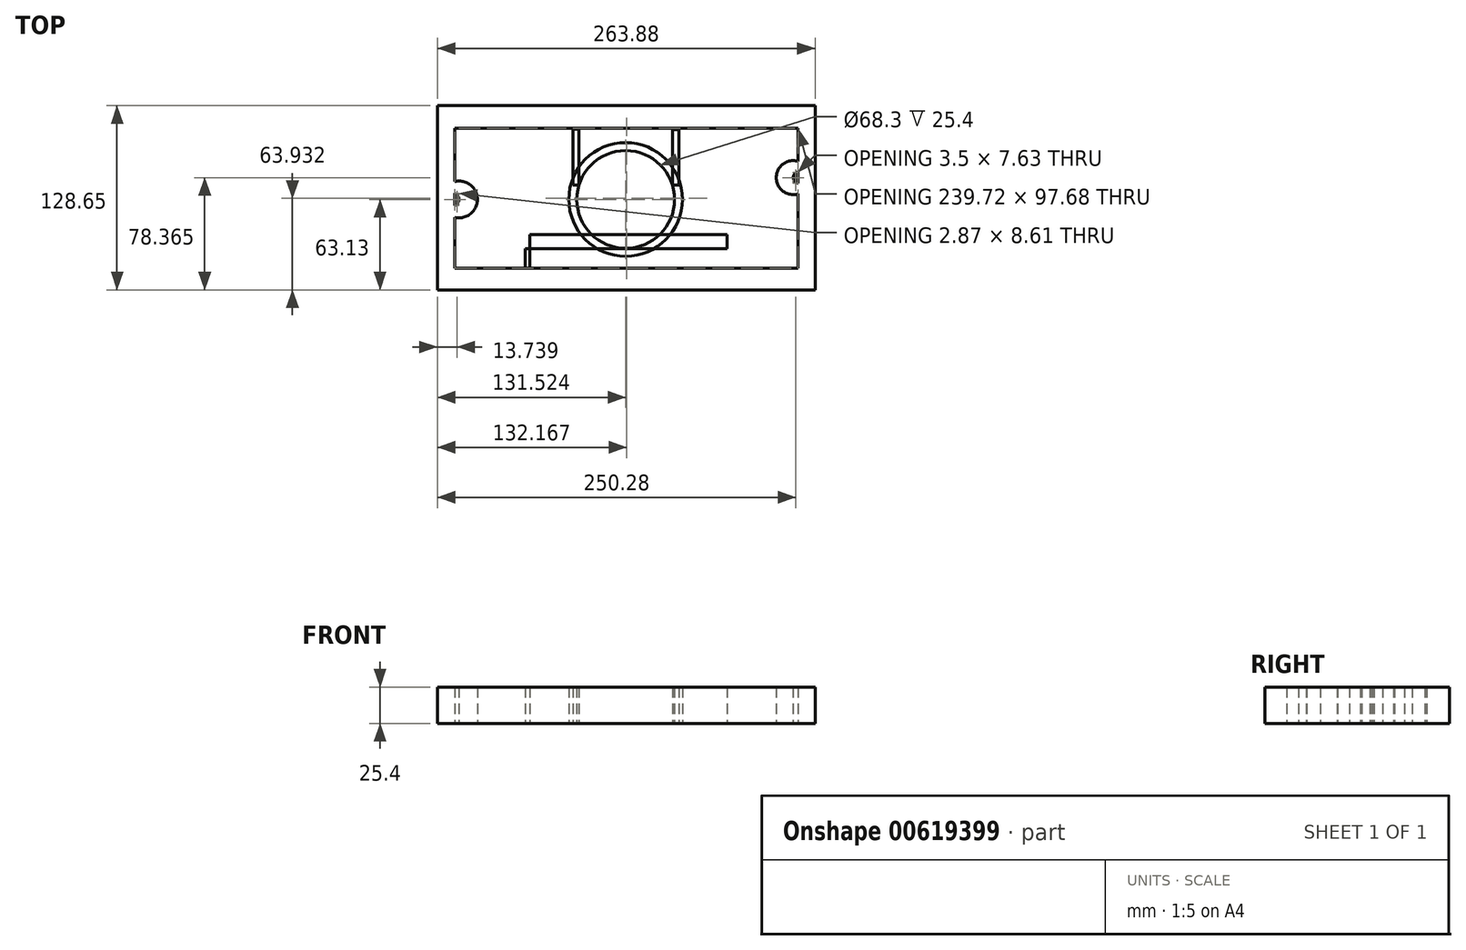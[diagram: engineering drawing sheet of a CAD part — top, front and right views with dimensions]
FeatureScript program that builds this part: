
annotation { "Feature Type Name" : "Feature", "Feature Type Description" : "" }
export const myFeature = defineFeature(function(context is Context, id is Id, definition is map)
    precondition{}
    {
        {
            var Q0;
            Q0=qCreatedBy(makeId("Top.planeOp"),FACE);
            var sketch = newSketch(context, id + "F0", { "sketchPlane" : qUnion([Q0])});
            skLineSegment(sketch, "E0.bottom", {"start": v(-134.85, 65.52) * mm, "end": v(129.03, 65.52) * mm});
            skLineSegment(sketch, "E0.top", {"start": v(-134.85, -63.13) * mm, "end": v(129.03, -63.13) * mm});
            skLineSegment(sketch, "E0.left", {"start": v(-134.85, 65.52) * mm, "end": v(-134.85, -63.13) * mm});
            skLineSegment(sketch, "E0.right", {"start": v(129.03, 65.52) * mm, "end": v(129.03, -63.13) * mm});
            skLineSegment(sketch, "E1.bottom", {"start": v(-122.54, 49.64) * mm, "end": v(117.18, 49.64) * mm});
            skLineSegment(sketch, "E1.top", {"start": v(-122.54, -48.04) * mm, "end": v(117.18, -48.04) * mm});
            skLineSegment(sketch, "E1.left", {"start": v(-122.54, 49.64) * mm, "end": v(-122.54, -48.04) * mm});
            skLineSegment(sketch, "E1.right", {"start": v(117.18, 49.64) * mm, "end": v(117.18, -48.04) * mm});
            skCircle(sketch, "E2", {"center": v(-115.43, 39.12) * mm, "radius": 5.88 * mm});
            skCircle(sketch, "E3", {"center": v(-115.43, -35.95) * mm, "radius": 4.5 * mm});
            skCircle(sketch, "E4", {"center": v(96.35, -31.86) * mm, "radius": 8.34 * mm});
            skCircle(sketch, "E5", {"center": v(97.11, 39.12) * mm, "radius": 6.34 * mm});
            skSolve(sketch);
        }
        {
            var Q0;
            Q0 = qSketchRegion(id + "F0", true);
            extrude(context, id + "F1", {"entities" : qUnion([Q0]), "depth" : 25.4 * mm, "offsetDistance" : 25.4 * mm});
        }
        {
            var Q0;
            Q0=qCreatedBy(makeId("Top.planeOp"),FACE);
            var sketch = newSketch(context, id + "F2", { "sketchPlane" : qUnion([Q0])});
            skCircle(sketch, "E6", {"center": v(-119.68, 43.9) * mm, "radius": 8.1 * mm});
            skCircle(sketch, "E7", {"center": v(-119.68, 43.9) * mm, "radius": 1.6 * mm});
            skCircle(sketch, "E8", {"center": v(82.83, 43.9) * mm, "radius": 9.97 * mm});
            skCircle(sketch, "E9", {"center": v(78.44, 43.9) * mm, "radius": 4.39 * mm});
            skCircle(sketch, "E10", {"center": v(-119.68, 0) * mm, "radius": 12.85 * mm});
            skCircle(sketch, "E11", {"center": v(-124.34, 0) * mm, "radius": 4.66 * mm});
            skCircle(sketch, "E12", {"center": v(77.24, 0) * mm, "radius": 6.36 * mm});
            skCircle(sketch, "E13", {"center": v(77.24, 0) * mm, "radius": 1.01 * mm});
            skSolve(sketch);
        }
        {
            var Q0;
            Q0=makeQuery(id+"F2.imprint","IMPRINT",FACE,{"disambiguationData":[TD([[makeQuery(id+"F2.imprint","IMPRINT",EDGE,{"derivedFrom":sQuery(id+"F2.wireOp",EDGE,"E10")}),1.0]])]});
            extrude(context, id + "F3", {"entities" : qUnion([Q0]), "operationType" : NewBodyOperationType.ADD, "depth" : 25.4 * mm, "offsetDistance" : 25.4 * mm});
        }
        {
            var Q0;
            Q0=qCreatedBy(makeId("Top.planeOp"),FACE);
            var sketch = newSketch(context, id + "F4", { "sketchPlane" : qUnion([Q0])});
            skCircle(sketch, "E14", {"center": v(113.68, 15.24) * mm, "radius": 11.84 * mm});
            skCircle(sketch, "E15", {"center": v(117.51, 15.24) * mm, "radius": 3.83 * mm});
            skSolve(sketch);
        }
        {
            var Q0;
            Q0=makeQuery(id+"F4.imprint","IMPRINT",FACE,{"disambiguationData":[TD([[makeQuery(id+"F4.imprint","IMPRINT",EDGE,{"derivedFrom":sQuery(id+"F4.wireOp",EDGE,"E14")}),1.0]])]});
            extrude(context, id + "F5", {"entities" : qUnion([Q0]), "operationType" : NewBodyOperationType.ADD, "depth" : 25.4 * mm, "offsetDistance" : 25.4 * mm});
        }
        {
            var Q0;
            Q0=qCreatedBy(makeId("Top.planeOp"),FACE);
            var sketch = newSketch(context, id + "F6", { "sketchPlane" : qUnion([Q0])});
            skLineSegment(sketch, "E16.bottom", {"start": v(-40.2, 48.99) * mm, "end": v(-36.09, 48.99) * mm});
            skLineSegment(sketch, "E16.top", {"start": v(-40.2, 10.02) * mm, "end": v(-36.09, 10.02) * mm});
            skLineSegment(sketch, "E16.left", {"start": v(-40.2, 48.99) * mm, "end": v(-40.2, 10.02) * mm});
            skLineSegment(sketch, "E16.right", {"start": v(-36.09, 48.99) * mm, "end": v(-36.09, 10.02) * mm});
            skLineSegment(sketch, "E17.bottom", {"start": v(33.98, 48.65) * mm, "end": v(29.53, 48.65) * mm});
            skLineSegment(sketch, "E17.top", {"start": v(33.98, 10.02) * mm, "end": v(29.53, 10.02) * mm});
            skLineSegment(sketch, "E17.left", {"start": v(33.98, 48.65) * mm, "end": v(33.98, 10.02) * mm});
            skLineSegment(sketch, "E17.right", {"start": v(29.53, 48.65) * mm, "end": v(29.53, 10.02) * mm});
            skLineSegment(sketch, "E18.bottom", {"start": v(-40.2, 53.09) * mm, "end": v(-36.09, 53.09) * mm});
            skLineSegment(sketch, "E18.left", {"start": v(-40.2, 53.09) * mm, "end": v(-40.2, 10.02) * mm});
            skLineSegment(sketch, "E18.right", {"start": v(-36.09, 53.09) * mm, "end": v(-36.09, 10.02) * mm});
            skLineSegment(sketch, "E19.bottom", {"start": v(29.53, 53.09) * mm, "end": v(33.98, 53.09) * mm});
            skLineSegment(sketch, "E19.top", {"start": v(29.53, 10.02) * mm, "end": v(33.98, 10.02) * mm});
            skLineSegment(sketch, "E19.left", {"start": v(29.53, 53.09) * mm, "end": v(29.53, 10.02) * mm});
            skLineSegment(sketch, "E19.right", {"start": v(33.98, 53.09) * mm, "end": v(33.98, 10.02) * mm});
            skSolve(sketch);
        }
        {
            var Q0;
            {var subQ0=sQuery(id+"F6.wireOp",EDGE,"E16.bottom");Q0=makeQuery(id+"F6.imprint","IMPRINT",FACE,{"disambiguationData":[TD([[makeQuery(id+"F6.imprint","IMPRINT",EDGE,{"derivedFrom":subQ0}),-1.0]])]});}
            var Q1;
            {var subQ0=sQuery(id+"F6.wireOp",EDGE,"E17.bottom");Q1=makeQuery(id+"F6.imprint","IMPRINT",FACE,{"disambiguationData":[TD([[makeQuery(id+"F6.imprint","IMPRINT",EDGE,{"derivedFrom":subQ0}),1.0]])]});}
            extrude(context, id + "F7", {"entities" : qUnion([Q0, Q1]), "depth" : 25.4 * mm, "offsetDistance" : 25.4 * mm});
        }
        {
            var Q0;
            Q0=qCreatedBy(makeId("Top.planeOp"),FACE);
            var sketch = newSketch(context, id + "F8", { "sketchPlane" : qUnion([Q0])});
            skCircle(sketch, "E20", {"center": v(-3.33, 0) * mm, "radius": 34.15 * mm});
            skCircle(sketch, "E21", {"center": v(-3.33, 0) * mm, "radius": 39.68 * mm});
            skSolve(sketch);
        }
        {
            var Q0;
            Q0=makeQuery(id+"F8.imprint","IMPRINT",FACE,{"disambiguationData":[TD([[makeQuery(id+"F8.imprint","IMPRINT",EDGE,{"derivedFrom":sQuery(id+"F8.wireOp",EDGE,"E20")}),-1.0]])]});
            extrude(context, id + "F9", {"entities" : qUnion([Q0]), "depth" : 25.4 * mm, "offsetDistance" : 25.4 * mm});
        }
        {
            var Q0;
            Q0=qCreatedBy(makeId("Top.planeOp"),FACE);
            var sketch = newSketch(context, id + "F10", { "sketchPlane" : qUnion([Q0])});
            skLineSegment(sketch, "E22.bottom", {"start": v(-70.17, -27.34) * mm, "end": v(67.39, -27.34) * mm});
            skLineSegment(sketch, "E22.top", {"start": v(-70.17, -34.37) * mm, "end": v(67.39, -34.37) * mm});
            skLineSegment(sketch, "E22.left", {"start": v(-70.17, -27.34) * mm, "end": v(-70.17, -34.37) * mm});
            skLineSegment(sketch, "E22.right", {"start": v(67.39, -27.34) * mm, "end": v(67.39, -34.37) * mm});
            skLineSegment(sketch, "E23.bottom", {"start": v(-73.33, -24.52) * mm, "end": v(70.2, -24.52) * mm});
            skLineSegment(sketch, "E23.top", {"start": v(-73.33, -34.37) * mm, "end": v(70.2, -34.37) * mm});
            skLineSegment(sketch, "E23.left", {"start": v(-73.33, -24.52) * mm, "end": v(-73.33, -34.37) * mm});
            skLineSegment(sketch, "E23.right", {"start": v(70.2, -24.52) * mm, "end": v(70.2, -34.37) * mm});
            skLineSegment(sketch, "E24.bottom", {"start": v(-73.33, -24.52) * mm, "end": v(-70.17, -24.52) * mm});
            skLineSegment(sketch, "E24.top", {"start": v(-73.33, -48.1) * mm, "end": v(-70.17, -48.1) * mm});
            skLineSegment(sketch, "E24.left", {"start": v(-73.33, -24.52) * mm, "end": v(-73.33, -48.1) * mm});
            skLineSegment(sketch, "E24.right", {"start": v(-70.17, -24.52) * mm, "end": v(-70.17, -48.1) * mm});
            skLineSegment(sketch, "E25.bottom", {"start": v(70.2, -24.52) * mm, "end": v(67.39, -24.52) * mm});
            skLineSegment(sketch, "E25.top", {"start": v(70.2, -48.1) * mm, "end": v(67.39, -48.1) * mm});
            skLineSegment(sketch, "E25.left", {"start": v(70.2, -24.52) * mm, "end": v(70.2, -48.1) * mm});
            skLineSegment(sketch, "E25.right", {"start": v(67.39, -24.52) * mm, "end": v(67.39, -48.1) * mm});
            skLineSegment(sketch, "E26.bottom", {"start": v(-73.33, -21.7) * mm, "end": v(-70.17, -21.7) * mm});
            skLineSegment(sketch, "E26.left", {"start": v(-73.33, -21.7) * mm, "end": v(-73.33, -48.1) * mm});
            skLineSegment(sketch, "E26.right", {"start": v(-70.17, -21.7) * mm, "end": v(-70.17, -48.1) * mm});
            skLineSegment(sketch, "E27.bottom", {"start": v(67.39, -21.35) * mm, "end": v(70.2, -21.35) * mm});
            skLineSegment(sketch, "E27.top", {"start": v(67.39, -48.1) * mm, "end": v(70.2, -48.1) * mm});
            skLineSegment(sketch, "E27.left", {"start": v(67.39, -21.35) * mm, "end": v(67.39, -48.1) * mm});
            skLineSegment(sketch, "E27.right", {"start": v(70.2, -21.35) * mm, "end": v(70.2, -48.1) * mm});
            skSolve(sketch);
        }
        {
            var Q0;
            {var subQ0=sQuery(id+"F10.wireOp",EDGE,"E22.bottom");Q0=makeQuery(id+"F10.imprint","IMPRINT",FACE,{"disambiguationData":[TD([[makeQuery(id+"F10.imprint","IMPRINT",EDGE,{"derivedFrom":subQ0}),-1.0]])]});}
            var Q1;
            {var subQ5=sQuery(id+"F10.wireOp",EDGE,"E24.top");Q1=makeQuery(id+"F10.imprint","IMPRINT",FACE,{"disambiguationData":[TD([[makeQuery(id+"F10.imprint","IMPRINT",EDGE,{"derivedFrom":subQ5}),1.0]])]});}
            var Q2;
            {var subQ2=sQuery(id+"F10.wireOp",EDGE,"E24.bottom");Q2=makeQuery(id+"F10.imprint","IMPRINT",FACE,{"disambiguationData":[TD([[makeQuery(id+"F10.imprint","IMPRINT",EDGE,{"derivedFrom":subQ2}),-1.0]])]});}
            var Q3;
            {var subQ5=sQuery(id+"F10.wireOp",EDGE,"E27.top");Q3=makeQuery(id+"F10.imprint","IMPRINT",FACE,{"disambiguationData":[TD([[makeQuery(id+"F10.imprint","IMPRINT",EDGE,{"derivedFrom":subQ5}),1.0]])]});}
            var Q4;
            {var subQ4=sQuery(id+"F10.wireOp",EDGE,"E25.bottom");Q4=makeQuery(id+"F10.imprint","IMPRINT",FACE,{"disambiguationData":[TD([[makeQuery(id+"F10.imprint","IMPRINT",EDGE,{"derivedFrom":subQ4}),1.0]])]});}
            var Q5;
            {var subQ0=sQuery(id+"F10.wireOp",EDGE,"E22.bottom");Q5=makeQuery(id+"F10.imprint","IMPRINT",FACE,{"disambiguationData":[TD([[makeQuery(id+"F10.imprint","IMPRINT",EDGE,{"derivedFrom":subQ0}),1.0]])]});}
            extrude(context, id + "F11", {"entities" : qUnion([Q0, Q1, Q2, Q3, Q4, Q5]), "depth" : 25.4 * mm, "offsetDistance" : 25.4 * mm});
        }
    });
